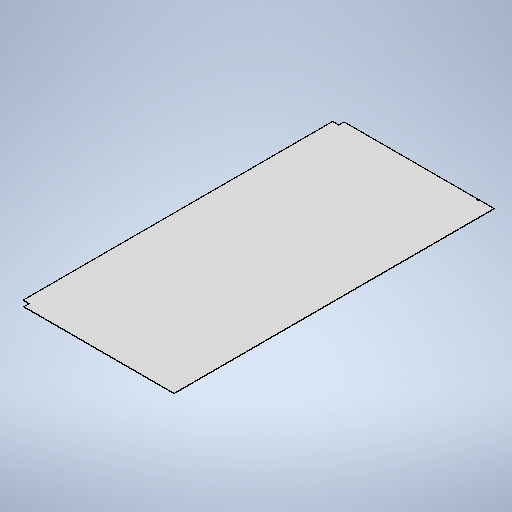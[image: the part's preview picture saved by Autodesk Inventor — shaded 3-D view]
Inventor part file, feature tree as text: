
AUTODESK INVENTOR PART (.ipt)
format: ipt  version: 2025.3 (Build 293356000, 356)  size: 297,984 bytes
history: native  units: mm
features: other x3, sketch x2, sheet_metal_op x1
ambient origin geometry x8: Origin, YZ Plane, XZ Plane, XY Plane, X Axis, Y Axis, Z Axis, Center Point
bodies: Solid1 (feature_tree)
feature tree (6):
  sheet_metal_op  "Face1"
  sketch  "Sketch1"  dims[d2=3.0mm]
  other  "Plate1"
  sketch  "Sketch5"  dims[d22=1025.0mm d23=2100.0mm d24=40.0mm d25=35.0mm d28=100.0mm d29=410.0mm d30=100.0mm d31=2.0mm d32=5.0mm d33=4.0mm d34=0.5mm d35=5.0mm d36=5.0mm d37=5.0mm d38=2.0mm d39=3.0mm d40=0.0mm]
  other  "Cut1"
  other  "Definition1"
